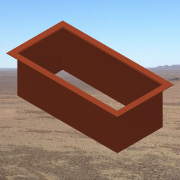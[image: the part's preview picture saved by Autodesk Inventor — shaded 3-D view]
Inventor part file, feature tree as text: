
AUTODESK INVENTOR PART (.ipt)
format: ipt  version: 2014 SP1 (Build 180222100, 222)  size: 136,704 bytes
history: native  units: in
note: dims shown in document units (in); Inventor stores cm internally (conversion verified against a paired STEP export)
features: extrude x3, sketch x3
ambient origin geometry x8: Origin, YZ Plane, XZ Plane, XY Plane, X Axis, Y Axis, Z Axis, Center Point
bodies: Solid1 (feature_tree)
feature tree (6):
  extrude  "Extrusion1"  Depth=10.0in
  extrude  "Extrusion2"  Depth=1.1811in
  extrude  "Extrusion4"  Depth=0.1in
  sketch  "Sketch1"  dims[d0=22.0in d1=10.0in]
  sketch  "Sketch2"  dims[d2=8.0in d3=0.0in d4=1.1811in]
  sketch  "Sketch4"  dims[d5=0.1in d6=0.0in d9=0.1in d10=9.9in d11=0.0in]
